# Revit family: Módulo de 32 salidas para información_Aguilera Electronica
name_source: partatom
category: Dispositivos de alarma de incendios
revit_build: Autodesk Revit 2017 (Build: 20160225_1515(x64)
units: mm (PartAtom-declared; Revit-internal decimal feet)

## family parameters
Anfitrión = Cara
Compartido = No
Corte con vacíos al cargar = No
Cota de conector redondo = Diámetro de uso
Mantener orientación de anotación = Sí
Número OmniClass = 23.85.30.21
Punto de cálculo de habitación = No
Tipo de pieza = Normal
Título OmniClass = Environmental Detection/Registration

## types (1)
- Módulo de 32 salidas para información
    Descripción = Unidad microprocesada direccionable fabricada por AGUILERA ELECTRÓNICA que gestiona y presenta información de la instalación en 32 salidas. Especial para configurar sinópticos, repetidores y cuadros de maniobras.
• Salida de la información por conector.
• Provisto de autoaislador que le aísla del resto de la instalación en caso de cortocircuito en su interior.
• Alimentación: entre 18 y 27 Vcc.
• Consumo: 1 mA.
• Conexión a 2 hilos con clemas extraíbles.
• Montado en caja de ABS de 105 x 82 x 25mm.
    Diámetro tubo = 20 mm  [stored 0.0656168 ft]
    Elevación por defecto = 1200 mm
    Fabricante = Aguilera Electrónica
    Modelo = AE/SA-32S
    Símbolo = Sí
    Símbolo texto modelo = Sí
    URL = http://aguilera.es

note: [stored X ft] marks values corroborated as IEEE doubles in the binary element streams (Revit-internal decimal feet)
